# Revit family: 208_USAV-_
name_source: partatom
category: Air Terminals
units: mm (PartAtom-declared; Revit-internal decimal feet)

## family parameters
Always vertical = Yes
Cut with Voids When Loaded = No
Part Type = Normal
Room Calculation Point = Yes
Round Connector Dimension = Use Diameter
Shared = No
Work Plane-Based = No

## types (10) — shared parameters
CAT0 = Yes
CL_Location_5000 = 5000 mm  [stored 16.4042 ft]
Description = ALUMINIUM AIR INTAKE WALL MOUNTED
L1 = 5 mm  [stored 0.0164042 ft]
L1__ve = -5 mm  [stored -0.0164042 ft]
L_ARR = 400 mm  [stored 1.31234 ft]
Manufacturer = Alnor
QmdConnectorList = 201;D
URL = http://www.ventilation-alnor.co.uk
W_ARR = 400 mm  [stored 1.31234 ft]
XRefLineVPlnId = 7453
YRefLineVPlnId = 7456
magiPartTypeId = 208
magiProductFamilyId = USAV-*
zero-valued in all types: CLBTZ, H_ARR

## per-type parameters (varying)
| type | D | DA | R | magiProductId |
| USAV 100 | 100 mm | 125 mm  [stored 0.410105 ft] | 50 mm  [stored 0.164042 ft] | USAV-100 |
| USAV 630 | 630 mm | 660 mm | 315 mm | USAV-630 |
| USAV 500 | 500 mm | 530 mm | 250 mm | USAV-500 |
| USAV 400 | 400 mm | 430 mm | 200 mm  [stored 0.656168 ft] | USAV-400 |
| USAV 315 | 315 mm | 350 mm | 158 mm | USAV-315 |
| USAV 250 | 250 mm | 275 mm | 125 mm  [stored 0.410105 ft] | USAV-250 |
| USAV 200 | 200 mm | 225 mm | 100 mm  [stored 0.328084 ft] | USAV-200 |
| USAV 160 | 160 mm | 185 mm | 80 mm | USAV-160 |
| USAV 150 | 150 mm | 175 mm | 75 mm | USAV-150 |
| USAV 125 | 125 mm | 150 mm | 63 mm | USAV-125 |

note: column(s) folded — value = type name in every type: MC Product Code

note: [stored X ft] marks values corroborated as IEEE doubles in the binary element streams (Revit-internal decimal feet)

## geometry (parser evidence)
native form markers: Blend x4, Sweep x1
no freeform markers — native parametric forms only
